# Revit family: 1801a_td300
name_source: partatom
category: Communication Devices
units: mm (PartAtom-declared; Revit-internal decimal feet)

## family parameters
Cut with Voids When Loaded = No
Host = Face
Maintain Annotation Orientation = No
OmniClass Number = 23.85.80.11.27
OmniClass Title = Lighting Controls
Part Type = Normal
Room Calculation Point = No
Round Connector Dimension = Use Diameter
Shared = Yes

## types (1)
- 1801a_td300
    Assembly Code = D5090
    Black = Paint - Carbon Black
    Default Elevation = 48 "
    Description = With its aesthetically pleasing features, the TD300 combines style with functionality as it provides energy saving control of incandescent and fluorescent lighting, as well as certain motor loads such as fans, hot tub heaters and circulating pumps.
    Features = Zero Arc Point Switching
• No minimum load requirement
• Adjustable time delay and sensitivity
• Walk test indicator
• Dual 120/277 VAC operation
• UL and cUL listed
• Title 24 compliant
• Five-year limited warranty
• 120-277 Vac
    Height = 4.5 "
    Manufacturer = NX Lighting Controls
    Model = Digital Programmable Timer
    Power Requirement = 120/230/277VAC; 50/60Hz
    Type Comments = POWER PACKS AND RELAYS
    URL = https://www.currentlighting.com
    Warranty = 5-Years Warranty
    White = Paint -  Matte White
    Width = 2.75 "

## geometry (parser evidence)
native form markers: Sweep x2
no freeform markers — native parametric forms only
